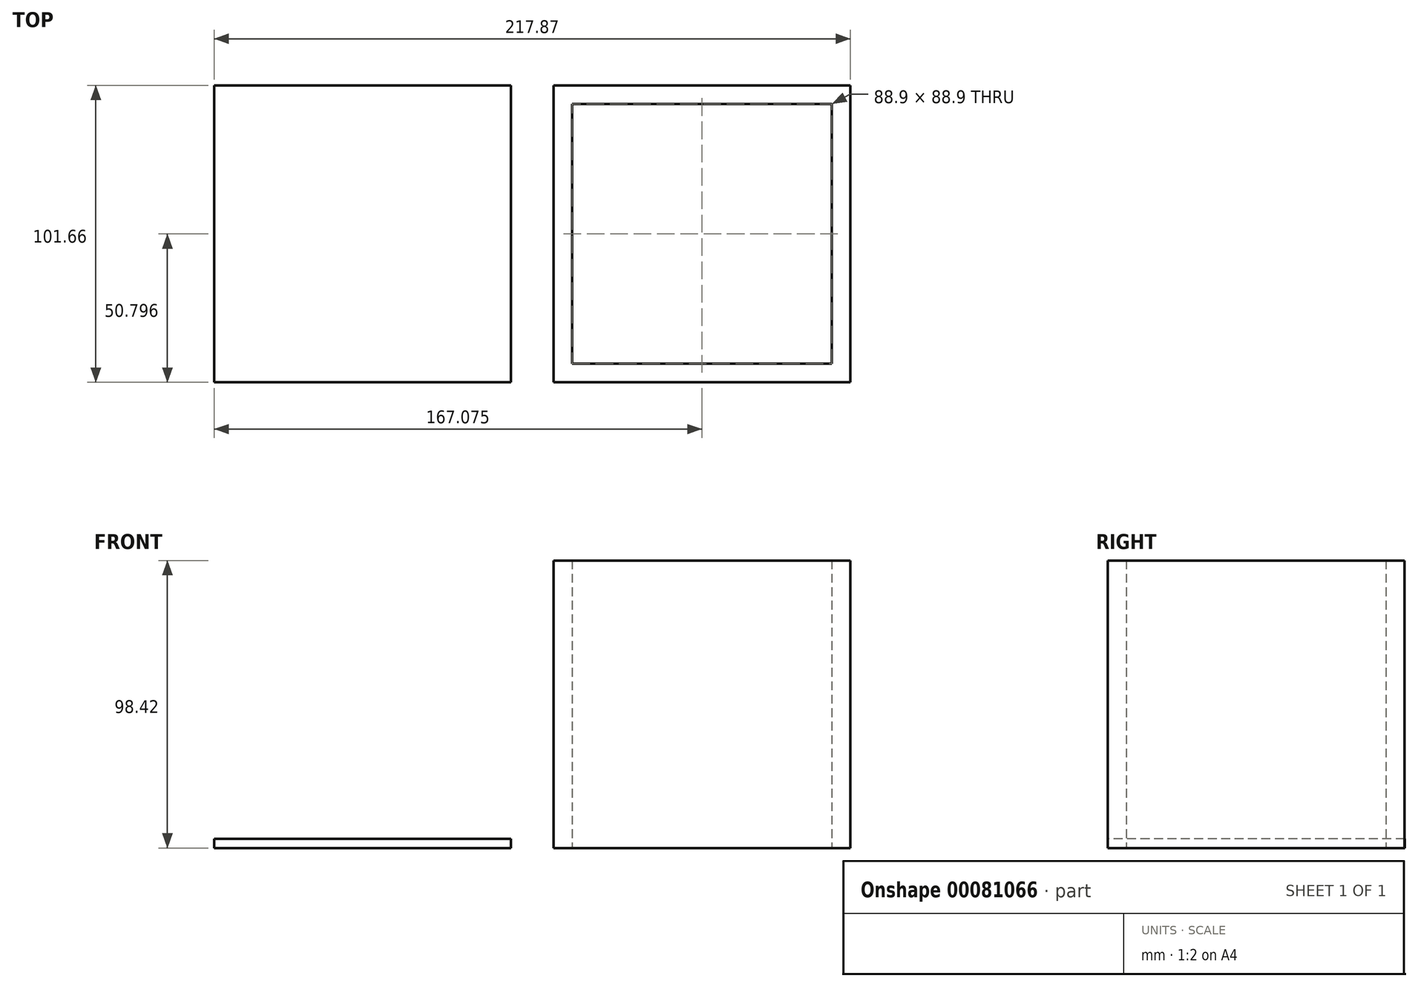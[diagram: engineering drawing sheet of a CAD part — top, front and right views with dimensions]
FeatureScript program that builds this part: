
annotation { "Feature Type Name" : "Feature", "Feature Type Description" : "" }
export const myFeature = defineFeature(function(context is Context, id is Id, definition is map)
    precondition{}
    {
        {
            var Q0;
            Q0=qCreatedBy(makeId("Top.planeOp"),FACE);
            var sketch = newSketch(context, id + "F0", { "sketchPlane" : qUnion([Q0])});
            skLineSegment(sketch, "E0.bottom", {"start": v(-11.22, 54.69) * mm, "end": v(90.38, 54.69) * mm});
            skLineSegment(sketch, "E0.top", {"start": v(-11.22, -46.91) * mm, "end": v(90.38, -46.91) * mm});
            skLineSegment(sketch, "E0.left", {"start": v(-11.22, 54.69) * mm, "end": v(-11.22, -46.91) * mm});
            skLineSegment(sketch, "E0.right", {"start": v(90.38, 54.69) * mm, "end": v(90.38, -46.91) * mm});
            skLineSegment(sketch, "E1.bottom", {"start": v(-127.49, 54.75) * mm, "end": v(-25.89, 54.75) * mm});
            skLineSegment(sketch, "E1.top", {"start": v(-127.49, -46.85) * mm, "end": v(-25.89, -46.85) * mm});
            skLineSegment(sketch, "E1.left", {"start": v(-127.49, 54.75) * mm, "end": v(-127.49, -46.85) * mm});
            skLineSegment(sketch, "E1.right", {"start": v(-25.89, 54.75) * mm, "end": v(-25.89, -46.85) * mm});
            skLineSegment(sketch, "E2.bottom", {"start": v(-4.87, 48.34) * mm, "end": v(84.03, 48.34) * mm});
            skLineSegment(sketch, "E2.top", {"start": v(-4.87, -40.56) * mm, "end": v(84.03, -40.56) * mm});
            skLineSegment(sketch, "E2.left", {"start": v(-4.87, 48.34) * mm, "end": v(-4.87, -40.56) * mm});
            skLineSegment(sketch, "E2.right", {"start": v(84.03, 48.34) * mm, "end": v(84.03, -40.56) * mm});
            skSolve(sketch);
        }
        {
            var Q0;
            Q0=makeQuery(id+"F0.imprint","IMPRINT",FACE,{"disambiguationData":[TD([[makeQuery(id+"F0.imprint","IMPRINT",EDGE,{"derivedFrom":sQuery(id+"F0.wireOp",EDGE,"E1.bottom")}),-1.0]])]});
            extrude(context, id + "F1", {"entities" : qUnion([Q0]), "depth" : 3.17 * mm});
        }
        {
            var Q0;
            Q0=makeQuery(id+"F0.imprint","IMPRINT",FACE,{"disambiguationData":[TD([[makeQuery(id+"F0.imprint","IMPRINT",EDGE,{"derivedFrom":sQuery(id+"F0.wireOp",EDGE,"E0.bottom")}),-1.0]])]});
            extrude(context, id + "F2", {"entities" : qUnion([Q0]), "depth" : 98.42 * mm});
        }
    });
